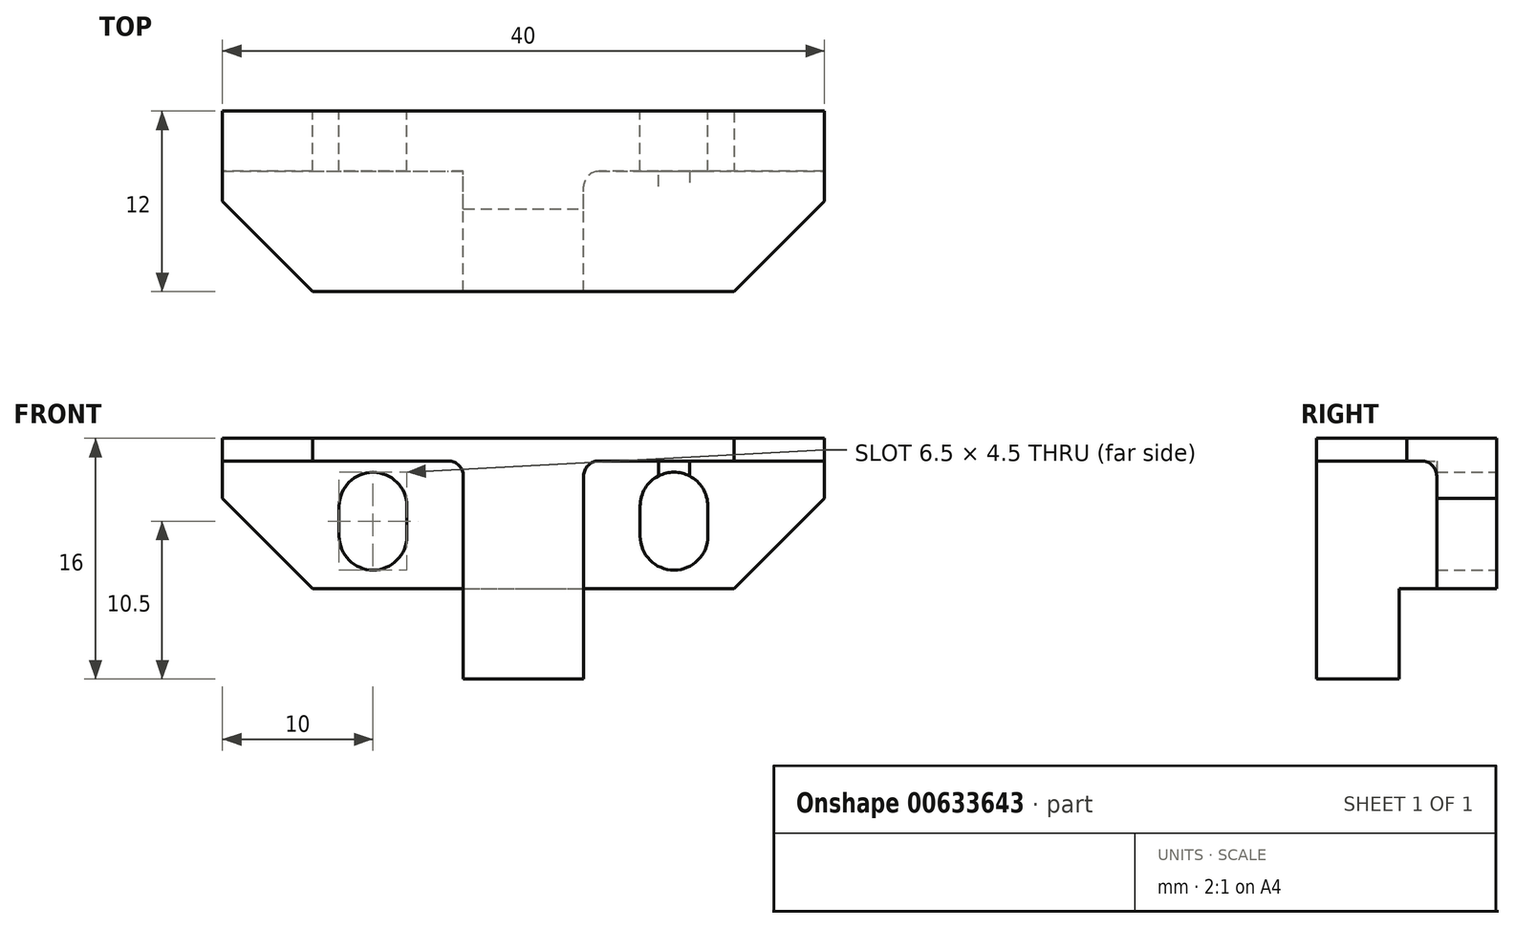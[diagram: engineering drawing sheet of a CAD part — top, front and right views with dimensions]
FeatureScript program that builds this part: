
annotation { "Feature Type Name" : "Feature", "Feature Type Description" : "" }
export const myFeature = defineFeature(function(context is Context, id is Id, definition is map)
    precondition{}
    {
        {
            var Q0;
            Q0=qCreatedBy(makeId("Front.planeOp"),FACE);
            var sketch = newSketch(context, id + "F0", { "sketchPlane" : qUnion([Q0])});
            skLineSegment(sketch, "E0.bottom", {"start": v(-20, 5) * mm, "end": v(20, 5) * mm});
            skLineSegment(sketch, "E0.left", {"start": v(-20, 5) * mm, "end": v(-20, -5) * mm});
            skLineSegment(sketch, "E0.right", {"start": v(20, 5) * mm, "end": v(20, -5) * mm});
            skPoint(sketch, "E1.startSnap0", {"position": v(0, 5) * mm});
            skPoint(sketch, "E1.endSnap0", {"position": v(0, 5) * mm});
            skLineSegment(sketch, "E2", {"start": v(-20, -5) * mm, "end": v(20, -5) * mm});
            skLineSegment(sketch, "E3", {"start": v(-12.25, 0.5) * mm, "end": v(-12.25, -1.5) * mm});
            skLineSegment(sketch, "E4", {"start": v(-7.75, 0.5) * mm, "end": v(-7.75, -1.5) * mm});
            skArc(sketch, "E5", {"start": v(-12.25, 0.5) * mm, "mid": v(-10, 2.75) * mm, "end": v(-7.75, 0.5) * mm});
            skArc(sketch, "E6", {"start": v(-12.25, -1.5) * mm, "mid": v(-10, -3.75) * mm, "end": v(-7.75, -1.5) * mm});
            skLineSegment(sketch, "E7", {"start": v(-13.37, -0.5) * mm, "end": v(-7.06, -0.5) * mm, "construction": true});
            skLineSegment(sketch, "E8", {"start": v(-10, 3.8) * mm, "end": v(-10, -4.8) * mm, "construction": true});
            skLineSegment(sketch, "E9.MirrorCS", {"start": v(12.25, 0.5) * mm, "end": v(12.25, -1.5) * mm});
            skArc(sketch, "E10.MirrorCS", {"start": v(12.25, -1.5) * mm, "mid": v(10, -3.75) * mm, "end": v(7.75, -1.5) * mm});
            skLineSegment(sketch, "E11.MirrorCS", {"start": v(10, 3.8) * mm, "end": v(10, -4.8) * mm, "construction": true});
            skLineSegment(sketch, "E12.MirrorCS", {"start": v(7.75, 0.5) * mm, "end": v(7.75, -1.5) * mm});
            skArc(sketch, "E13.MirrorCS", {"start": v(12.25, 0.5) * mm, "mid": v(10, 2.75) * mm, "end": v(7.75, 0.5) * mm});
            skSolve(sketch);
        }
        {
            var Q0;
            Q0=makeQuery(id+"F0.imprint","IMPRINT",FACE,{"disambiguationData":[TD([[makeQuery(id+"F0.imprint","IMPRINT",EDGE,{"derivedFrom":sQuery(id+"F0.wireOp",EDGE,"E0.bottom")}),-1.0]])]});
            extrude(context, id + "F1", {"entities" : qUnion([Q0]), "depth" : 4 * mm, "offsetDistance" : 25 * mm});
        }
        {
            var Q0;
            Q0=makeQuery(id+"F1.opExtrude","CAP_FACE",FACE,{"disambiguationData":[OSD([sQuery(id+"F0.wireOp",EDGE,"E0.bottom"),sQuery(id+"F0.wireOp",EDGE,"E0.top"),sQuery(id+"F0.wireOp",EDGE,"E0.left"),sQuery(id+"F0.wireOp",EDGE,"E0.right"),sQuery(id+"F0.wireOp",EDGE,"ea225624-6685-4acc-8dc6-de662683e1a85.MirrorCS"),sQuery(id+"F0.wireOp",EDGE,"ea225624-6685-4acc-8dc6-de662683e1a88.MirrorCS"),sQuery(id+"F0.wireOp",EDGE,"ea225624-6685-4acc-8dc6-de662683e1a810.MirrorCS"),sQuery(id+"F0.wireOp",EDGE,"ea225624-6685-4acc-8dc6-de662683e1a813.MirrorCS"),sQuery(id+"F0.wireOp",EDGE,"ea225624-6685-4acc-8dc6-de662683e1a814.MirrorCS"),sQuery(id+"F0.wireOp",EDGE,"80049206-fc12-4322-b61f-103c15692f4b2.MirrorCS"),sQuery(id+"F0.wireOp",EDGE,"80049206-fc12-4322-b61f-103c15692f4b6.MirrorCS"),sQuery(id+"F0.wireOp",EDGE,"80049206-fc12-4322-b61f-103c15692f4b9.MirrorCS"),sQuery(id+"F0.wireOp",EDGE,"80049206-fc12-4322-b61f-103c15692f4b13.MirrorCS"),sQuery(id+"F0.wireOp",EDGE,"80049206-fc12-4322-b61f-103c15692f4b15.MirrorCS"),sQuery(id+"F0.wireOp",EDGE,"80049206-fc12-4322-b61f-103c15692f4b16.MirrorCS")])],"isStart":false});
            var sketch = newSketch(context, id + "F2", { "sketchPlane" : qUnion([Q0])});
            skLineSegment(sketch, "E14.bottom", {"start": v(-4, 5) * mm, "end": v(4, 5) * mm});
            skLineSegment(sketch, "E14.top", {"start": v(-4, -5) * mm, "end": v(4, -5) * mm});
            skLineSegment(sketch, "E14.left", {"start": v(-4, 5) * mm, "end": v(-4, -5) * mm});
            skLineSegment(sketch, "E14.right", {"start": v(4, 5) * mm, "end": v(4, -5) * mm});
            skLineSegment(sketch, "E15.bottom", {"start": v(-20, 5) * mm, "end": v(-4, 5) * mm});
            skLineSegment(sketch, "E15.top", {"start": v(-20, 3.5) * mm, "end": v(-4, 3.5) * mm});
            skLineSegment(sketch, "E15.left", {"start": v(-20, 5) * mm, "end": v(-20, 3.5) * mm});
            skLineSegment(sketch, "E15.right", {"start": v(-4, 5) * mm, "end": v(-4, 3.5) * mm});
            skLineSegment(sketch, "E16.bottom", {"start": v(20, 5) * mm, "end": v(4, 5) * mm});
            skLineSegment(sketch, "E16.top", {"start": v(20, 3.5) * mm, "end": v(4, 3.5) * mm});
            skLineSegment(sketch, "E16.left", {"start": v(20, 5) * mm, "end": v(20, 3.5) * mm});
            skLineSegment(sketch, "E16.right", {"start": v(4, 5) * mm, "end": v(4, 3.5) * mm});
            skSolve(sketch);
        }
        {
            var Q0;
            Q0=makeQuery(id+"F2.imprint","IMPRINT",FACE,{"disambiguationData":[TD([[makeQuery(id+"F2.imprint","IMPRINT",EDGE,{"derivedFrom":sQuery(id+"F2.wireOp",EDGE,"7HP3edu6-lnOT-jCw5-6FpB-wS7vSzKiooAZ.bottom")}),-1.0]])]});
            var Q1;
            Q1=makeQuery(id+"F2.imprint","IMPRINT",FACE,{"disambiguationData":[TD([[makeQuery(id+"F2.imprint","IMPRINT",EDGE,{"derivedFrom":sQuery(id+"F2.wireOp",EDGE,"E14.bottom")}),-1.0]])]});
            var Q2;
            Q2=makeQuery(id+"F2.imprint","IMPRINT",FACE,{"disambiguationData":[TD([[makeQuery(id+"F2.imprint","IMPRINT",EDGE,{"derivedFrom":sQuery(id+"F2.wireOp",EDGE,"E15.bottom")}),-1.0]])]});
            var Q3;
            Q3=makeQuery(id+"F2.imprint","IMPRINT",FACE,{"disambiguationData":[TD([[makeQuery(id+"F2.imprint","IMPRINT",EDGE,{"derivedFrom":sQuery(id+"F2.wireOp",EDGE,"E16.bottom")}),-1.0]])]});
            extrude(context, id + "F3", {"entities" : qUnion([Q0, Q1, Q2, Q3]), "operationType" : NewBodyOperationType.ADD, "depth" : 8 * mm, "offsetDistance" : 25 * mm});
        }
        {
            var Q0;
            Q0=makeQuery(id+"F3.boolean.opBoolean","MERGE",FACE,{"derivedFrom":[makeQuery(id+"F1.opExtrude","SWEPT_FACE",FACE,{"disambiguationData":[OSD([sQuery(id+"F0.wireOp",EDGE,"E2")])]}),makeQuery(id+"F3.opExtrude","SWEPT_FACE",FACE,{"disambiguationData":[OSD([sQuery(id+"F2.wireOp",EDGE,"E14.top")])]})]});
            var sketch = newSketch(context, id + "F4", { "sketchPlane" : qUnion([Q0])});
            skLineSegment(sketch, "E17.bottom", {"start": v(-4, 12) * mm, "end": v(4, 12) * mm});
            skLineSegment(sketch, "E17.top", {"start": v(-4, 6.5) * mm, "end": v(4, 6.5) * mm});
            skLineSegment(sketch, "E17.left", {"start": v(-4, 12) * mm, "end": v(-4, 6.5) * mm});
            skLineSegment(sketch, "E17.right", {"start": v(4, 12) * mm, "end": v(4, 6.5) * mm});
            skSolve(sketch);
        }
        {
            var Q0;
            Q0 = qSketchRegion(id + "F4", true);
            var Q1;
            {var subQ0=sQuery(id+"F4.wireOp",EDGE,"jzmHSP7v-8JG1-SSry-WmSH-hWYO7qOIVdhW");Q1=makeQuery(id+"F4.imprint","IMPRINT",FACE,{"disambiguationData":[TD([[makeQuery(id+"F4.imprint","IMPRINT",EDGE,{"derivedFrom":subQ0}),1.0]])]});}
            extrude(context, id + "F5", {"entities" : qUnion([Q0, Q1]), "operationType" : NewBodyOperationType.ADD, "depth" : 6 * mm, "offsetDistance" : 25 * mm});
        }
        {
            var Q0;
            Q0=makeQuery(id+"F3.opExtrude","CAP_EDGE",EDGE,{"disambiguationData":[OSD([sQuery(id+"F2.wireOp",EDGE,"E14.right")])],"isStart":true});
            var Q1;
            Q1=makeQuery(id+"F3.opExtrude","CAP_EDGE",EDGE,{"disambiguationData":[OSD([sQuery(id+"F2.wireOp",EDGE,"E14.left")])],"isStart":true});
            var Q2;
            Q2=makeQuery(id+"F3.opExtrude","CAP_EDGE",EDGE,{"disambiguationData":[OSD([sQuery(id+"F2.wireOp",EDGE,"E15.top")])],"isStart":true});
            var Q3;
            Q3=makeQuery(id+"F3.opExtrude","CAP_EDGE",EDGE,{"disambiguationData":[OSD([sQuery(id+"F2.wireOp",EDGE,"E16.top")])],"isStart":true});
            var Q4;
            Q4=makeQuery(id+"F3.opExtrude","SWEPT_EDGE",EDGE,{"disambiguationData":[OSD([sQuery(id+"F2.wireOp",EDGE,"E14.right"),sQuery(id+"F2.wireOp",EDGE,"E16.top"),sQuery(id+"F2.wireOp",EDGE,"E16.right")])]});
            var Q5;
            Q5=makeQuery(id+"F3.opExtrude","SWEPT_EDGE",EDGE,{"disambiguationData":[OSD([sQuery(id+"F2.wireOp",EDGE,"E14.left"),sQuery(id+"F2.wireOp",EDGE,"E15.top"),sQuery(id+"F2.wireOp",EDGE,"E15.right")])]});
            fillet(context, id + "F6", {"entities" : qUnion([Q0, Q1, Q2, Q3, Q4, Q5]), "radius" : 1 * mm, "tangentPropagation" : true, "allowEdgeOverflow" : false});
        }
        {
            var Q0;
            Q0=makeQuery(id+"F3.opExtrude","CAP_EDGE",EDGE,{"disambiguationData":[OSD([sQuery(id+"F2.wireOp",EDGE,"E15.left")])],"isStart":false});
            var Q1;
            Q1=makeQuery(id+"F3.opExtrude","CAP_EDGE",EDGE,{"disambiguationData":[OSD([sQuery(id+"F2.wireOp",EDGE,"E16.left")])],"isStart":false});
            var Q2;
            Q2=makeQuery(id+"F1.opExtrude","SWEPT_EDGE",EDGE,{"disambiguationData":[OSD([sQuery(id+"F0.wireOp",EDGE,"E0.right"),sQuery(id+"F0.wireOp",EDGE,"E2")])]});
            var Q3;
            Q3=makeQuery(id+"F1.opExtrude","SWEPT_EDGE",EDGE,{"disambiguationData":[OSD([sQuery(id+"F0.wireOp",EDGE,"E0.left"),sQuery(id+"F0.wireOp",EDGE,"E2")])]});
            chamfer(context, id + "F7", {"entities" : qUnion([Q0, Q1, Q2, Q3]), "width" : 6 * mm, "tangentPropagation" : true});
        }
    });
